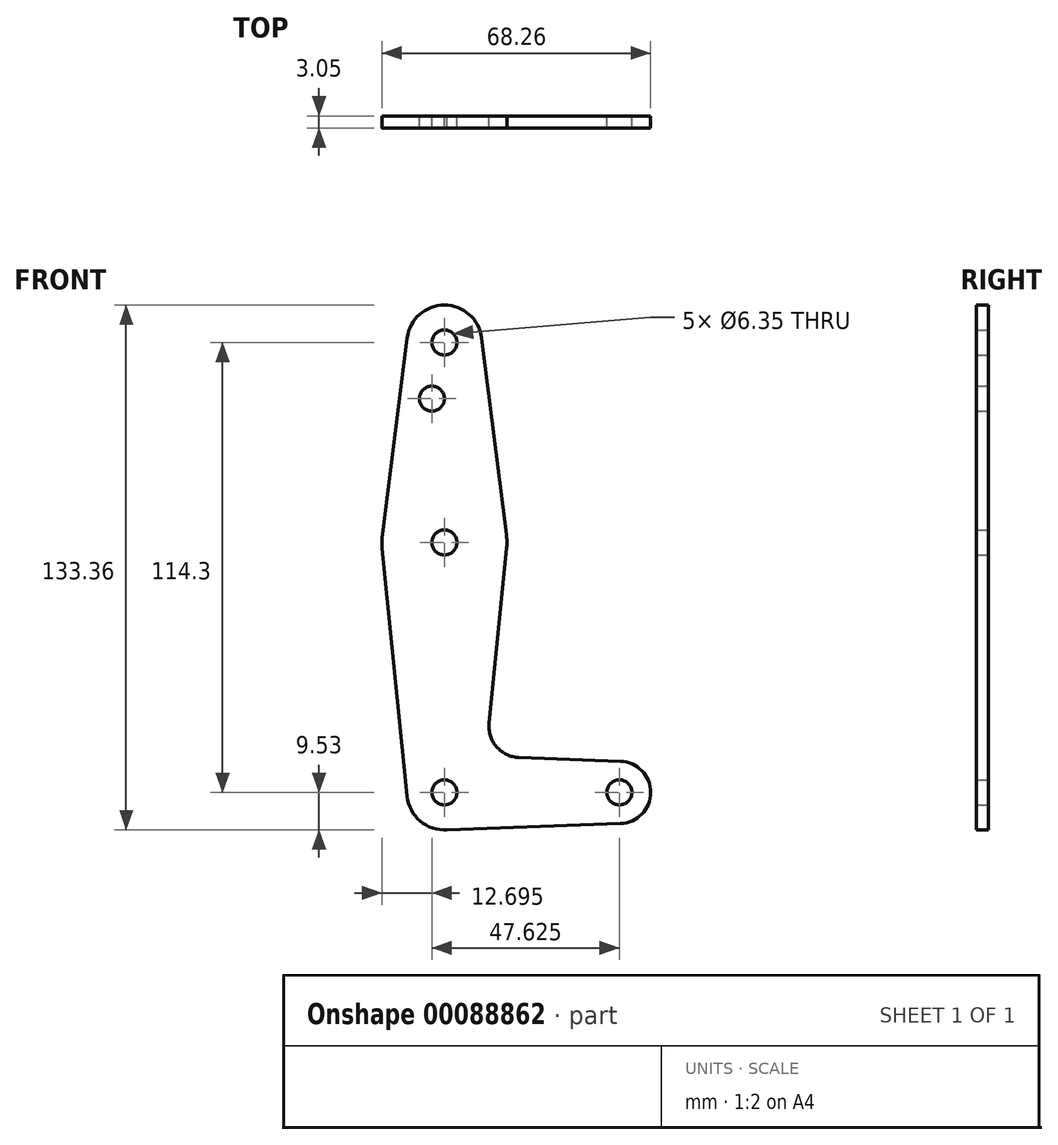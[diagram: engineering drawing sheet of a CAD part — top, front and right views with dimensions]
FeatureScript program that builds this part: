
annotation { "Feature Type Name" : "Feature", "Feature Type Description" : "" }
export const myFeature = defineFeature(function(context is Context, id is Id, definition is map)
    precondition{}
    {
        {
            var Q0;
            Q0=qCreatedBy(makeId("Front.planeOp"),FACE);
            var sketch = newSketch(context, id + "F0", { "sketchPlane" : qUnion([Q0])});
            skLineSegment(sketch, "E0", {"start": v(0, 114.3) * mm, "end": v(0, 0) * mm, "construction": true});
            skLineSegment(sketch, "E1", {"start": v(0, 0) * mm, "end": v(44.45, 0) * mm, "construction": true});
            skCircle(sketch, "E2", {"center": v(0, 114.3) * mm, "radius": 9.53 * mm});
            skCircle(sketch, "E3", {"center": v(0, 63.5) * mm, "radius": 15.88 * mm});
            skCircle(sketch, "E4", {"center": v(0, 0) * mm, "radius": 9.53 * mm});
            skCircle(sketch, "E5", {"center": v(44.45, 0) * mm, "radius": 7.94 * mm});
            skLineSegment(sketch, "E6", {"start": v(9.45, 115.5) * mm, "end": v(15.75, 65.48) * mm});
            skLineSegment(sketch, "E7", {"start": v(-9.45, 115.5) * mm, "end": v(-15.75, 65.48) * mm});
            skLineSegment(sketch, "E8", {"start": v(0, -9.53) * mm, "end": v(44.73, -7.93) * mm});
            skLineSegment(sketch, "E9", {"start": v(-15.8, 61.91) * mm, "end": v(-9.48, -0.95) * mm});
            skLineSegment(sketch, "E10", {"start": v(15.8, 61.91) * mm, "end": v(11.34, 17.6) * mm});
            skCircle(sketch, "E11", {"center": v(0, 114.3) * mm, "radius": 3.18 * mm});
            skCircle(sketch, "E12", {"center": v(0, 63.5) * mm, "radius": 3.18 * mm});
            skCircle(sketch, "E13", {"center": v(0, 0) * mm, "radius": 3.18 * mm});
            skCircle(sketch, "E14", {"center": v(44.45, 0) * mm, "radius": 3.18 * mm});
            skCircle(sketch, "E15", {"center": v(-3.17, 100.03) * mm, "radius": 3.18 * mm});
            skLineSegment(sketch, "E16", {"start": v(18.97, 8.85) * mm, "end": v(44.73, 7.93) * mm});
            skArc(sketch, "E17.filletArc", {"start": v(11.34, 17.6) * mm, "mid": v(13.26, 11.57) * mm, "end": v(18.97, 8.85) * mm});
            skSolve(sketch);
        }
        {
            var Q0;
            Q0 = qSketchRegion(id + "F0", true);
            extrude(context, id + "F1", {"entities" : qUnion([Q0]), "depth" : 3.05 * mm});
        }
    });
